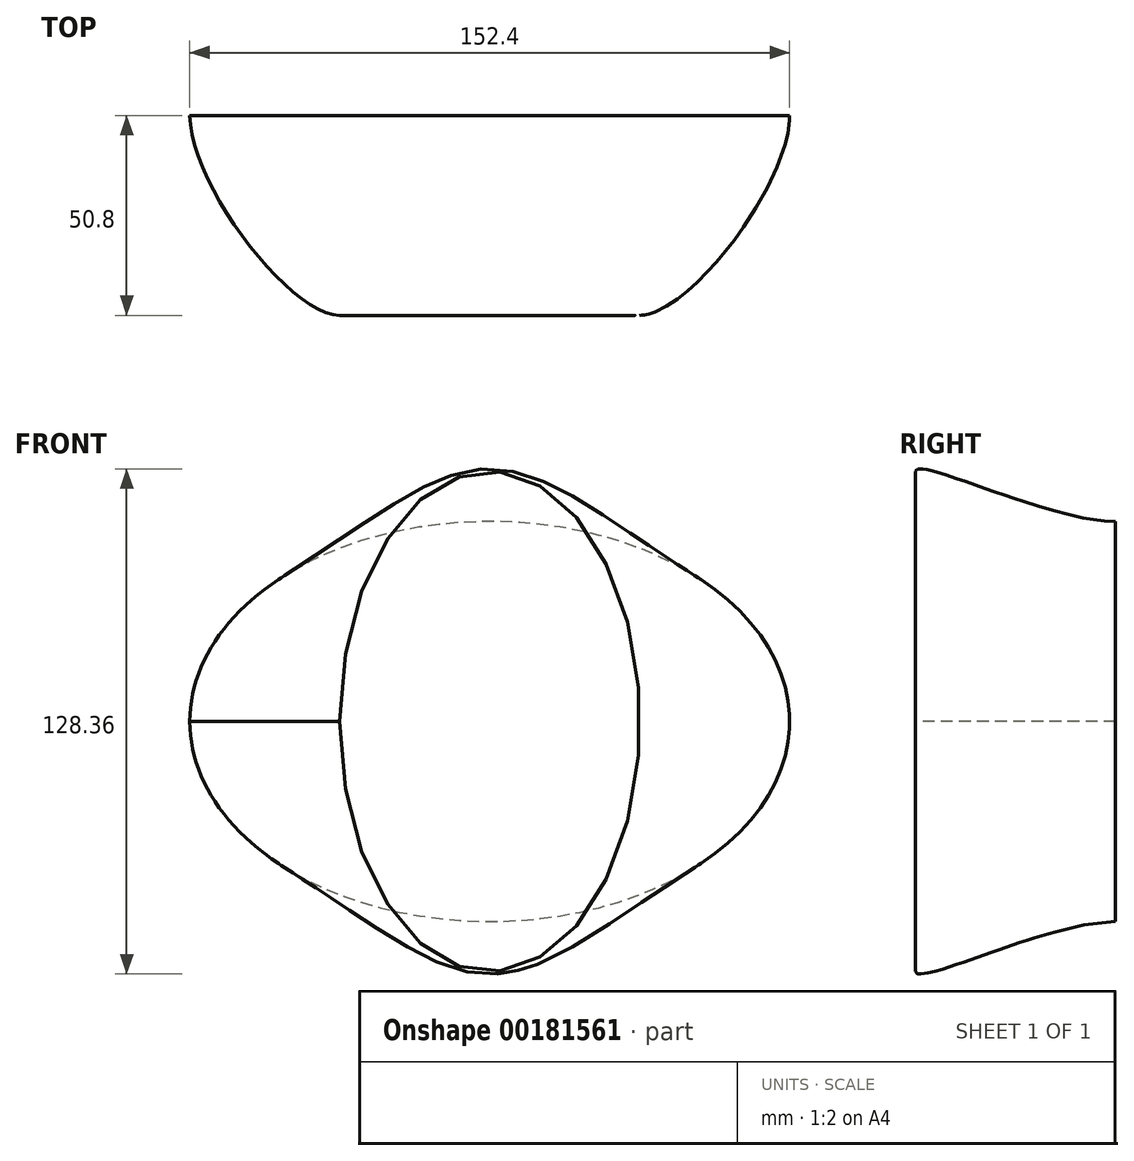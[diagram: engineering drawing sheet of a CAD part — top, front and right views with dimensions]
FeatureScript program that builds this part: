
annotation { "Feature Type Name" : "Feature", "Feature Type Description" : "" }
export const myFeature = defineFeature(function(context is Context, id is Id, definition is map)
    precondition{}
    {
        {
            var Q0;
            Q0=qCreatedBy(makeId("Front.planeOp"),FACE);
            var sketch = newSketch(context, id + "F0", { "sketchPlane" : qUnion([Q0])});
            skEllipse(sketch, "E0", {"center": v(0, 0) * mm, "majorRadius": 50.8 * mm, "minorRadius": 76.2 * mm, "majorAxis": v(0, 1)});
            skSolve(sketch);
        }
        {
            var Q0;
            Q0=qCreatedBy(makeId("Front.planeOp"),FACE);
            cPlane(context, id + "F1", {"entities" : qUnion([Q0]), "cplaneType" : CPlaneType.OFFSET, "offset" : 50.8 * mm, "width" : 152.4 * mm, "height" : 152.4 * mm});
        }
        {
            var Q0;
            Q0=qCreatedBy(id+"F1.planeOp",FACE);
            var sketch = newSketch(context, id + "F2", { "sketchPlane" : qUnion([Q0])});
            skEllipse(sketch, "E1", {"center": v(0, 0) * mm, "majorRadius": 63.5 * mm, "minorRadius": 38.1 * mm, "majorAxis": v(0, 1)});
            skSolve(sketch);
        }
        {
            var Q0;
            Q0=makeQuery(id+"F0.imprint","IMPRINT",FACE,{"disambiguationData":[TD([[makeQuery(id+"F0.imprint","IMPRINT",EDGE,{"derivedFrom":sQuery(id+"F0.wireOp",EDGE,"E0")}),1.0]])]});
            var Q1;
            Q1=makeQuery(id+"F2.imprint","IMPRINT",FACE,{"disambiguationData":[TD([[makeQuery(id+"F2.imprint","IMPRINT",EDGE,{"derivedFrom":sQuery(id+"F2.wireOp",EDGE,"E1")}),1.0]])]});
            loft(context, id + "F3", {"startCondition" : LoftEndDerivativeType.NORMAL_TO_PROFILE, "startMagnitude" : 1, "endCondition" : LoftEndDerivativeType.TANGENT_TO_PROFILE, "endMagnitude" : 1, "sheetProfilesArray" : [{ "sheetProfileEntities" : qUnion([Q0]) }, { "sheetProfileEntities" : qUnion([Q1]) }]});
        }
    });
